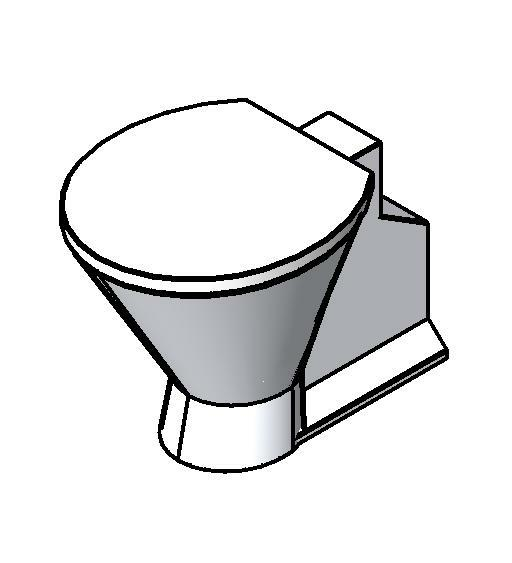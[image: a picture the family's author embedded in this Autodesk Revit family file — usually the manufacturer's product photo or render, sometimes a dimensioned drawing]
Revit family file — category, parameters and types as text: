
# Revit family: Deca_Acionamento monocomando mesa quadrada_Deca You_4990.105
name_source: partatom
category: Plumbing Fixtures
units: mm (PartAtom-declared; Revit-internal decimal feet)

## family parameters
Cut with Voids When Loaded = No
Host = Face
Part Type = Normal
Room Calculation Point = No
Round Connector Dimension = Use Radius
Shared = No

## types (11) — shared parameters
Acompanha o Produto = Flexiveis e Adaptadores de Rosca
Aprovado por = quattroD
Atendimento ao Cliente = 0800-0117073
Categoria = Acionamento  Monoc Lavatório / Banheiro
Composição Básica = Liga de Cobre (Latão),Plásticos de Engenharia, Aço Inoxidavel e Elastômeros
Consumo = -
Cor Secundária = -
Criado por = quattroD
Itens de Instalação = Mangueira Flexivel
Linha = Deca You
Manufacturer = DECA
Norma = Não possui
Pressão mín. Aquec. Acúmulo = -
Pressão mín. Aquec. Passagem = -
Saída de Esgoto = -
Segmento = Luxo
Tipo de dispositivo economizador = -
Tipo de mecanismo utilizado = Cartucho moncomando Rotativo
Tipo de rosca de entrada = BSP
Tipo de rosca de saída = BSP
URL = www.deca.com.br
zero-valued in all types: CWFU, Default Elevation, Diâmetro Ponto de Esgoto, Diâmetro Água Fria, Peso Líquido (Kg), Raio Ponto de Esgoto, Raio Água Fria, WFU

## per-type parameters (varying)
| type | Cor Principal | Código Pai | Material | Model |
| 4990.C105_Cromado | Cromado | 4990.C105 | Deca_Cromado | 4990.C105 |
| 4990.BL105.MT_Black Matte | Black Matte | 4990.BL105.MT | Deca_Black Matte | 4990.BL105.MT |
| 4990.GF105.MT_Grafite | Antracite Dark | 4990.GF105.MT | Deca_Grafite | 4990.GF105.MT |
| 4990.INX105_Inox | Inox | 4990.INX105 | Deca_Inox | 4990.INX105 |
| 4990.MR105.MT_Brown Matte | BROWN MATTE | 4990.MR105.MT | Deca_Brown Matte | 4990.MR105.MT |
| 4990.SM105.MT_Summer Gold | SUMMER GOLD | 4990.SM105.MT | Deca_Summer Gold | 4990.SM105.MT |
| 4990.BR105.MT_Dynamic White | Dynamic White | 4990.BR105.MT | Deca_Dynamic White | 4990.BR105.MT |
| 4990.LS105.MT_Dynamic Gold | Dynamic Gold | 4990.LS105.MT | Deca_Dynamic Gold | 4990.LS105.MT |
| 4990.CL105.MT_Dynamic Peach | Dynamic Peach | 4990.CL105.MT | Deca_Dynamic Peach | 4990.CL105.MT |
| 4990.LV105.MT_Dynamic Lilac | Dynamic Lilac | 4990.LV105.MT | Deca_Dynamic Lilac | 4990.LV105.MT |
| 4990.AZ105.MT_Dynamic Blue | Dynamic Blue | 4990.AZ105.MT | Deca_Dynamic Blue | 4990.AZ105.MT |

## geometry (parser evidence)
native form markers: Sweep x2
no freeform markers — native parametric forms only
